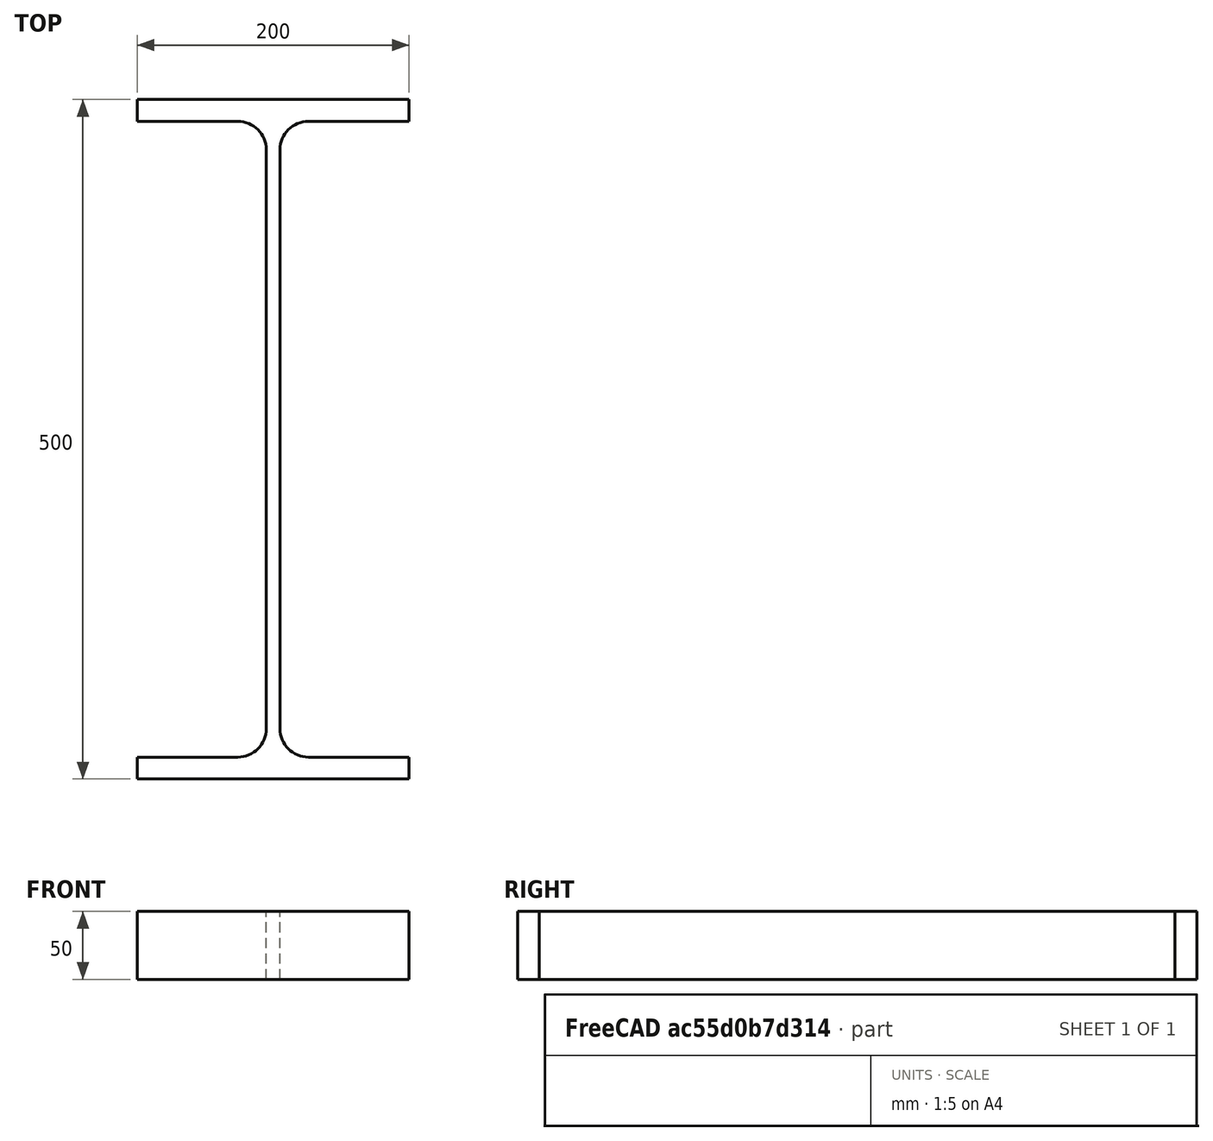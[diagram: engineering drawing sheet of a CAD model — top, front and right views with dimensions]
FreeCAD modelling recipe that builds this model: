
FCSTD DOCUMENT  (FreeCAD 0.15R4671 (Git))
Label: IPE-Profile 500 DIN1025-5 S235JR
License: All rights reserved
LicenseURL: http://en.wikipedia.org/wiki/All_rights_reserved
objects: Sketcher::SketchObject×1, Part::Extrusion×1
note: 2 computed .brp shape members not serialized (recipe doc carries the construction recipe); baked Part::Feature solids carry a one-line shape summary decoded from their .brp

FEATURE [Sketcher::SketchObject] Sketch
  sketch-geometry (16):
    g0: LineSegment StartX=5.1 StartY=-213 StartZ=0 EndX=5.1 EndY=213 EndZ=0
    g1: LineSegment StartX=26.1 StartY=234 StartZ=0 EndX=100 EndY=234 EndZ=0
    g2: LineSegment StartX=100 StartY=234 StartZ=0 EndX=100 EndY=250 EndZ=0
    g3: LineSegment StartX=100 StartY=250 StartZ=0 EndX=-100 EndY=250 EndZ=0
    g4: LineSegment StartX=-100 StartY=250 StartZ=0 EndX=-100 EndY=234 EndZ=0
    g5: LineSegment StartX=-100 StartY=234 StartZ=0 EndX=-26.1 EndY=234 EndZ=0
    g6: LineSegment StartX=-5.1 StartY=213 StartZ=0 EndX=-5.1 EndY=-213 EndZ=0
    g7: LineSegment StartX=-26.1 StartY=-234 StartZ=0 EndX=-100 EndY=-234 EndZ=0
    g8: LineSegment StartX=-100 StartY=-234 StartZ=0 EndX=-100 EndY=-250 EndZ=0
    g9: LineSegment StartX=-100 StartY=-250 StartZ=0 EndX=100 EndY=-250 EndZ=0
    g10: LineSegment StartX=100 StartY=-250 StartZ=0 EndX=100 EndY=-234 EndZ=0
    g11: LineSegment StartX=100 StartY=-234 StartZ=0 EndX=26.1 EndY=-234 EndZ=0
    g12: ArcOfCircle CenterX=26.1 CenterY=213 CenterZ=0 NormalX=0 NormalY=0 NormalZ=1 Radius=21 StartAngle=1.5708 EndAngle=3.14159
    g13: ArcOfCircle CenterX=26.1 CenterY=-213 CenterZ=0 NormalX=0 NormalY=0 NormalZ=1 Radius=21 StartAngle=3.14159 EndAngle=4.71239
    g14: ArcOfCircle CenterX=-26.1 CenterY=213 CenterZ=0 NormalX=0 NormalY=0 NormalZ=1 Radius=21 StartAngle=0 EndAngle=1.5708
    g15: ArcOfCircle CenterX=-26.1 CenterY=-213 CenterZ=0 NormalX=0 NormalY=0 NormalZ=1 Radius=21 StartAngle=4.71239 EndAngle=6.28319
  constraints (42):
    c: Vertical(g0)
    c: Coincident(g2,g1)
    c: Vertical(g2)
    c: Coincident(g3,g2)
    c: Coincident(g4,g3)
    c: Vertical(g4)
    c: Coincident(g5,g4)
    c: Horizontal(g5)
    c: Vertical(g6)
    c: Horizontal(g7)
    c: Coincident(g8,g7)
    c: Vertical(g8)
    c: Coincident(g9,g8)
    c: Horizontal(g9)
    c: Coincident(g10,g9)
    c: Vertical(g10)
    c: Coincident(g11,g10)
    c: Horizontal(g11)
    c: Tangent(g1,g12) = 1.5708
    c: Tangent(g0,g12) = 1.5708
    c: Tangent(g0,g13) = 1.5708
    c: Tangent(g11,g13) = 1.5708
    c: Tangent(g5,g14) = 1.5708
    c: Tangent(g6,g14) = 1.5708
    c: Tangent(g6,g15) = 1.5708
    c: Tangent(g7,g15) = 1.5708
    c: Equal(g3,g9)
    c: Equal(g2,g4)
    c: Equal(g4,g8)
    c: Equal(g8,g10)
    c: Equal(g12,g14)
    c: Equal(g14,g15)
    c: Equal(g15,g13)
    c: Symmetric(g2,g3,g-2)
    c: Symmetric(g9,g8,g-2)
    c: Symmetric(g0,g6,g-2)
    c: Symmetric(g2,g9,g-1)
    c: DistanceY(g2,g9) = -500
    c: DistanceX(g3) = -200
    c: DistanceX(g0,g6) = -10.2
    c: DistanceY(g2) = 16
    c: Radius(g12) = 21
FEATURE [Part::Extrusion] Extrude  label="IPE-Profile 500 DIN1025-5 S235JR"
  Base = -> Sketch
  Dir = (0,0,50)
  Solid = true
